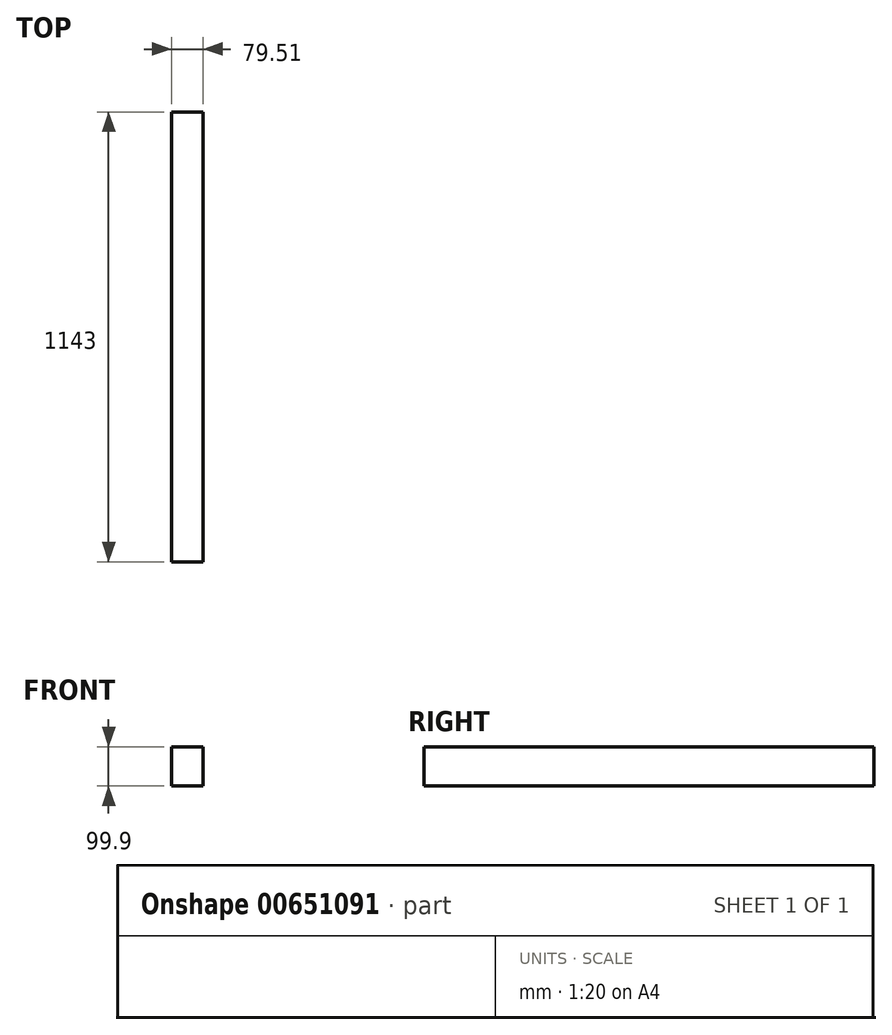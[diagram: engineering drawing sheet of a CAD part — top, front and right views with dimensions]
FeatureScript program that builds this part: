
annotation { "Feature Type Name" : "Feature", "Feature Type Description" : "" }
export const myFeature = defineFeature(function(context is Context, id is Id, definition is map)
    precondition{}
    {
        {
            var Q0;
            Q0=qCreatedBy(makeId("Front.planeOp"),FACE);
            var sketch = newSketch(context, id + "F0", { "sketchPlane" : qUnion([Q0])});
            skLineSegment(sketch, "E0.bottom", {"start": v(25.8, -140.46) * mm, "end": v(-53.7, -140.46) * mm});
            skLineSegment(sketch, "E0.top", {"start": v(25.8, -40.56) * mm, "end": v(-53.7, -40.56) * mm});
            skLineSegment(sketch, "E0.left", {"start": v(25.8, -140.46) * mm, "end": v(25.8, -40.56) * mm});
            skLineSegment(sketch, "E0.right", {"start": v(-53.7, -140.46) * mm, "end": v(-53.7, -40.56) * mm});
            skSolve(sketch);
        }
        {
            var Q0;
            Q0 = qSketchRegion(id + "F0", true);
            extrude(context, id + "F1", {"entities" : qUnion([Q0]), "depth" : 1143 * mm, "offsetDistance" : 25.4 * mm});
        }
    });
